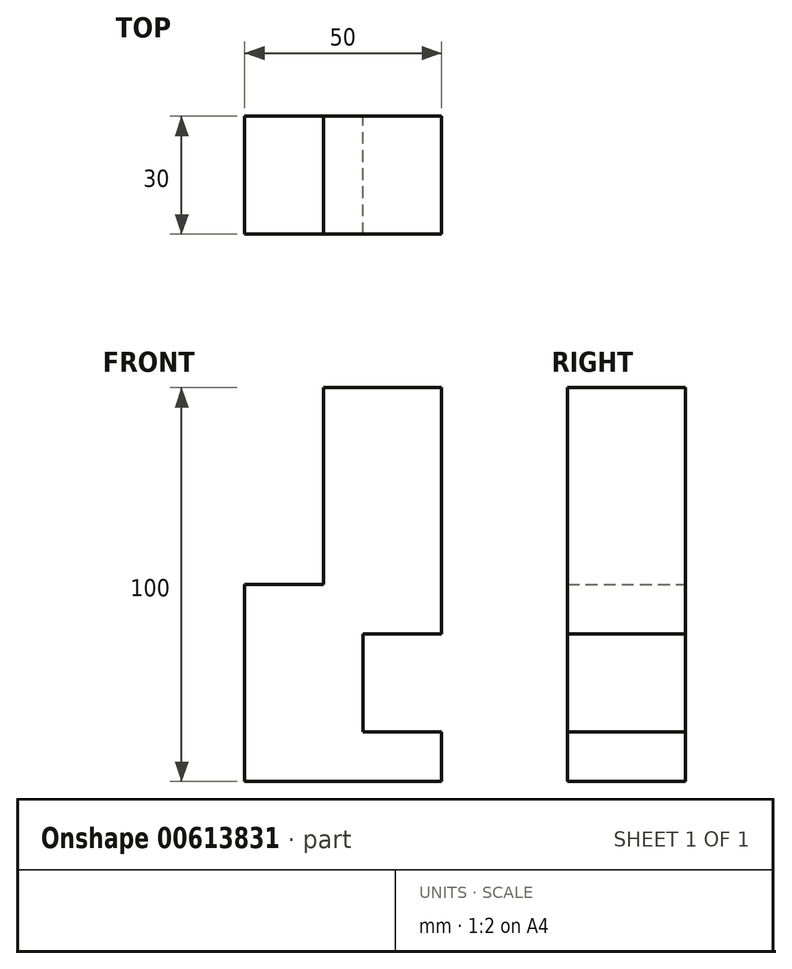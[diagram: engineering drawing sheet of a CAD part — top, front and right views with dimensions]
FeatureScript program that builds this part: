
annotation { "Feature Type Name" : "Feature", "Feature Type Description" : "" }
export const myFeature = defineFeature(function(context is Context, id is Id, definition is map)
    precondition{}
    {
        {
            var Q0;
            Q0=qCreatedBy(makeId("Front.planeOp"),FACE);
            var sketch = newSketch(context, id + "F0", { "sketchPlane" : qUnion([Q0])});
            skLineSegment(sketch, "E0", {"start": v(-14.3, 58.07) * mm, "end": v(15.7, 58.07) * mm});
            skLineSegment(sketch, "E1", {"start": v(15.7, 58.07) * mm, "end": v(15.7, -4.43) * mm});
            skLineSegment(sketch, "E2", {"start": v(15.7, -41.93) * mm, "end": v(-34.3, -41.93) * mm});
            skLineSegment(sketch, "E3", {"start": v(-34.3, -41.93) * mm, "end": v(-34.3, 8.07) * mm});
            skLineSegment(sketch, "E4", {"start": v(-34.3, 8.07) * mm, "end": v(-14.3, 8.07) * mm});
            skLineSegment(sketch, "E5", {"start": v(-14.3, 8.07) * mm, "end": v(-14.3, 58.07) * mm});
            skLineSegment(sketch, "E6", {"start": v(15.7, -4.43) * mm, "end": v(-4.3, -4.43) * mm});
            skLineSegment(sketch, "E7", {"start": v(-4.3, -4.43) * mm, "end": v(-4.3, -29.43) * mm});
            skLineSegment(sketch, "E8", {"start": v(-4.3, -29.43) * mm, "end": v(15.7, -29.43) * mm});
            skLineSegment(sketch, "E9.trimOffspring", {"start": v(15.7, -29.43) * mm, "end": v(15.7, -41.93) * mm});
            skSolve(sketch);
        }
        {
            var Q0;
            Q0=makeQuery(id+"F0.imprint","IMPRINT",FACE,{"disambiguationData":[TD([[makeQuery(id+"F0.imprint","IMPRINT",EDGE,{"derivedFrom":sQuery(id+"F0.wireOp",EDGE,"E0")}),-1.0]])]});
            extrude(context, id + "F1", {"entities" : qUnion([Q0]), "depth" : 30 * mm, "offsetDistance" : 25 * mm});
        }
    });
